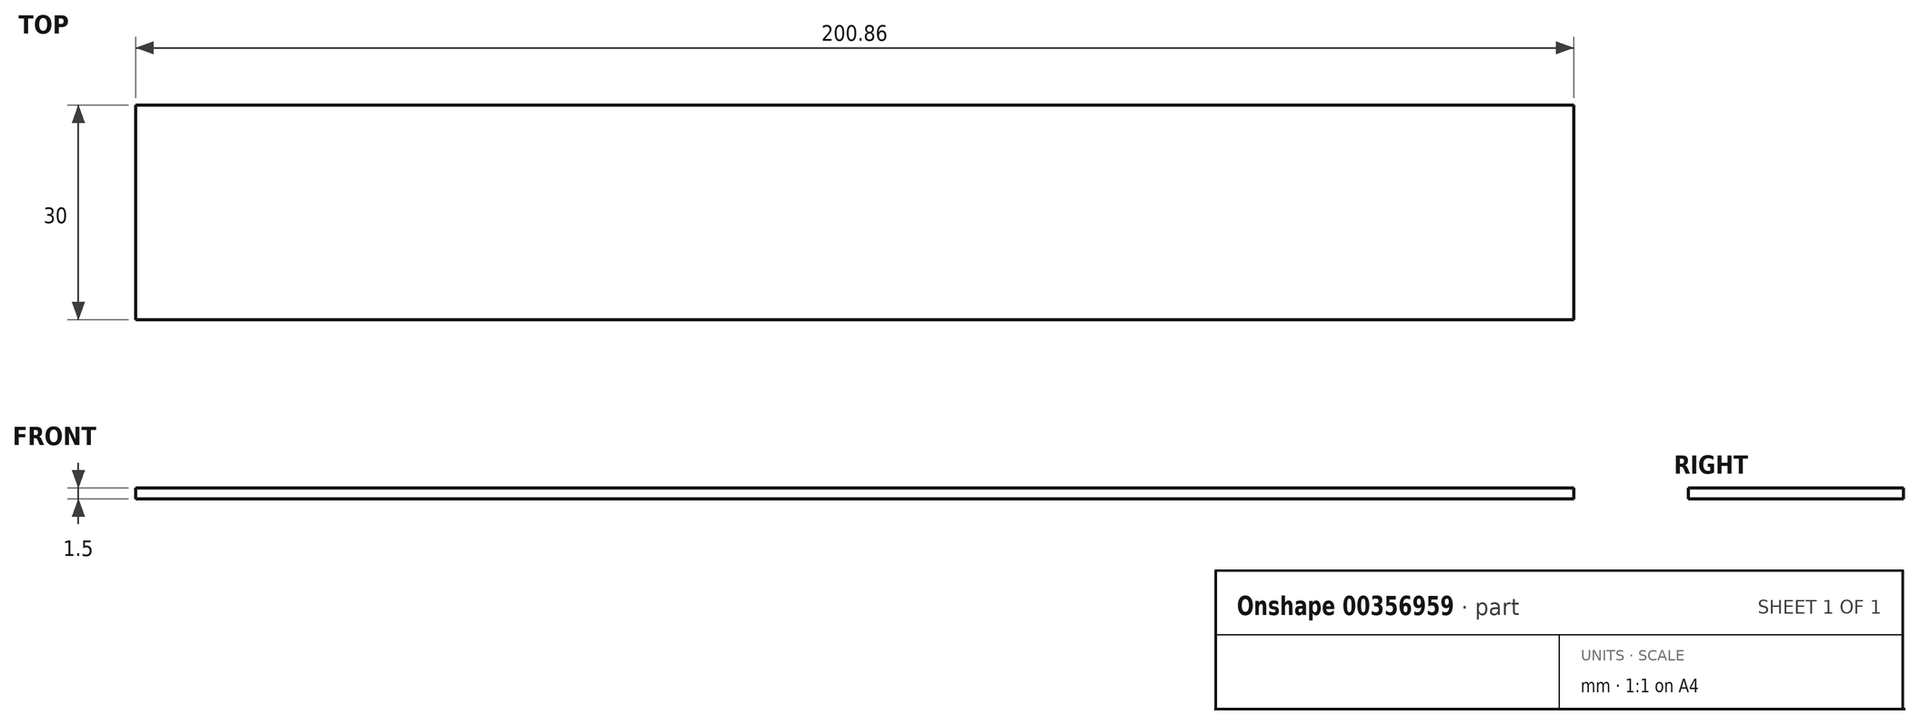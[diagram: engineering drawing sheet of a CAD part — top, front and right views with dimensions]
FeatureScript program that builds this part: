
annotation { "Feature Type Name" : "Feature", "Feature Type Description" : "" }
export const myFeature = defineFeature(function(context is Context, id is Id, definition is map)
    precondition{}
    {
        {
            var Q0;
            Q0=qCreatedBy(makeId("Top.planeOp"),FACE);
            var sketch = newSketch(context, id + "F0", { "sketchPlane" : qUnion([Q0])});
            skLineSegment(sketch, "E0.bottom", {"start": v(125.35, 2.72) * mm, "end": v(-75.51, 2.72) * mm});
            skLineSegment(sketch, "E0.top", {"start": v(125.35, -27.28) * mm, "end": v(-75.51, -27.28) * mm});
            skLineSegment(sketch, "E0.left", {"start": v(125.35, 2.72) * mm, "end": v(125.35, -27.28) * mm});
            skLineSegment(sketch, "E0.right", {"start": v(-75.51, 2.72) * mm, "end": v(-75.51, -27.28) * mm});
            skSolve(sketch);
        }
        {
            var Q0;
            Q0 = qSketchRegion(id + "F0", true);
            extrude(context, id + "F1", {"entities" : qUnion([Q0]), "depth" : 1.5 * mm});
        }
    });
